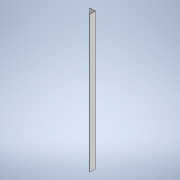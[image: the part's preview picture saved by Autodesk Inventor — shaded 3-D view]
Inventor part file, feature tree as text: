
AUTODESK INVENTOR PART (.ipt)
format: ipt  version: 2020.1 (Build 241239000, 239)  size: 97,280 bytes
history: native  units: mm
features: other x1, extrude x1, sketch x1
ambient origin geometry x8: Origin, YZ Plane, XZ Plane, XY Plane, X Axis, Y Axis, Z Axis, Center Point
bodies: Body1 (feature_tree)
feature tree (3):
  other  "Твердое тело1"
  extrude  "Выдавливание1"  Depth=3.0mm
  sketch  "Эскиз1"
